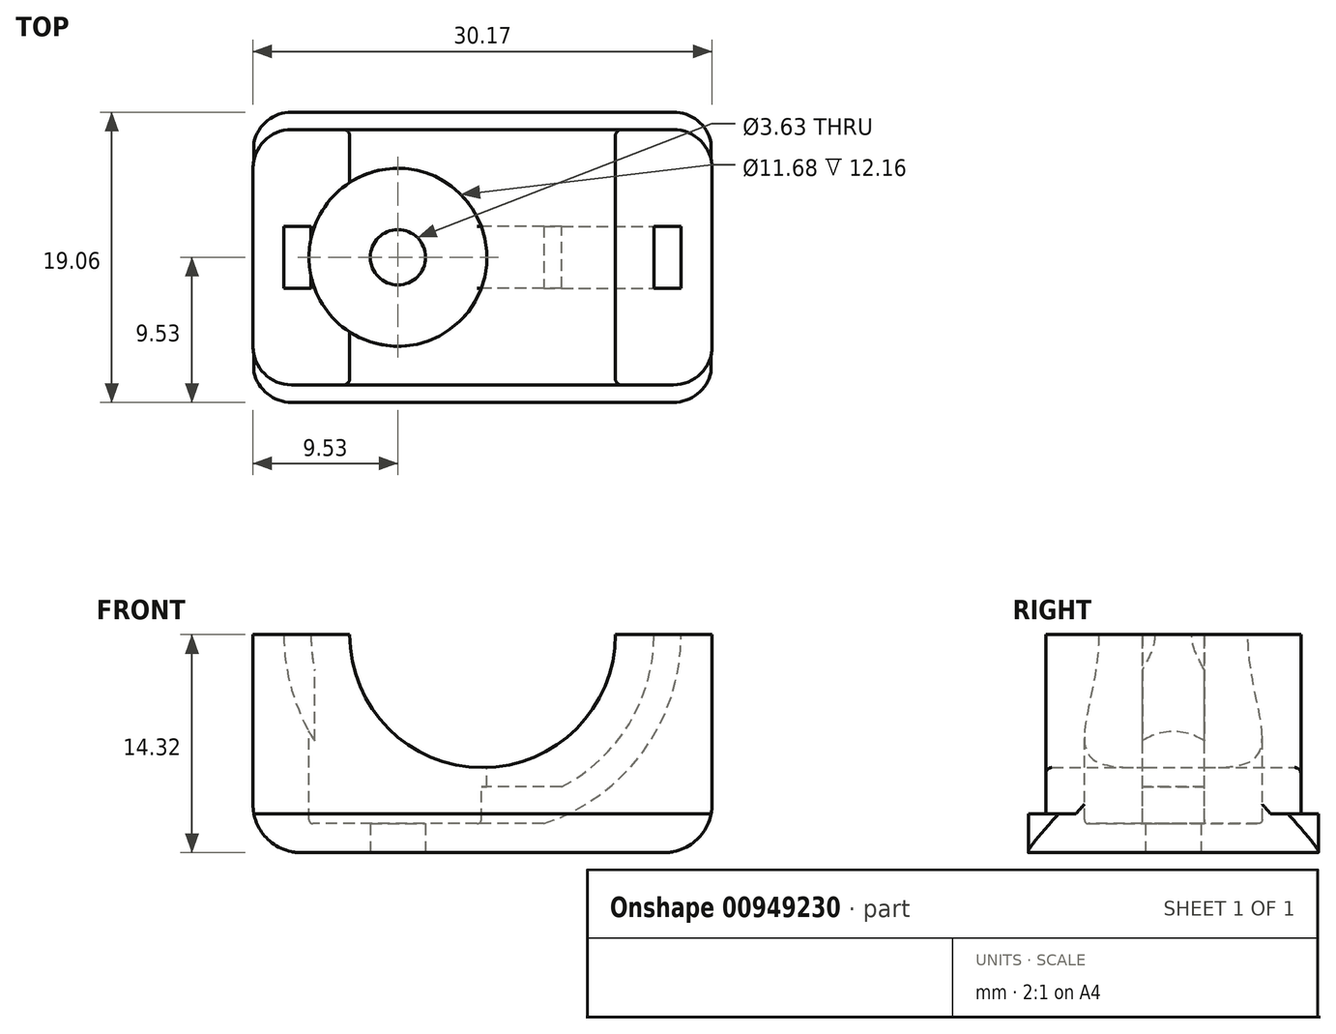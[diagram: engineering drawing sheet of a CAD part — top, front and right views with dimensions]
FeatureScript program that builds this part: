
annotation { "Feature Type Name" : "Feature", "Feature Type Description" : "" }
export const myFeature = defineFeature(function(context is Context, id is Id, definition is map)
    precondition{}
    {
        {
            assignVariable(context, id + "F0", {"name" : "TieWidth", "anyValue" : 4.06 * mm});
        }
        {
            assignVariable(context, id + "F1", {"name" : "RivetThick", "anyValue" : 1.9 * mm});
        }
        {
            var Q0;
            Q0=qCreatedBy(makeId("Top.planeOp"),FACE);
            var sketch = newSketch(context, id + "F2", { "sketchPlane" : qUnion([Q0])});
            skLineSegment(sketch, "E0.bottom", {"start": v(20.64, -9.53) * mm, "end": v(-9.53, -9.53) * mm});
            skLineSegment(sketch, "E0.top", {"start": v(20.64, 9.52) * mm, "end": v(-9.53, 9.52) * mm});
            skLineSegment(sketch, "E0.left", {"start": v(20.64, -9.53) * mm, "end": v(20.64, 9.53) * mm});
            skLineSegment(sketch, "E0.right", {"start": v(-9.53, -9.53) * mm, "end": v(-9.53, 9.53) * mm});
            skPoint(sketch, "E0.middle", {"position": v(0, 0) * mm});
            skPoint(sketch, "E1.visualSharp", {"position": v(-9.53, 9.53) * mm});
            skPoint(sketch, "E2.visualSharp", {"position": v(20.64, 9.53) * mm});
            skPoint(sketch, "E3.visualSharp", {"position": v(20.64, -9.53) * mm});
            skPoint(sketch, "E4.visualSharp", {"position": v(-9.53, -9.53) * mm});
            skCircle(sketch, "E5", {"center": v(0, 0) * mm, "radius": 1.82 * mm});
            skCircle(sketch, "E6", {"center": v(0, 0) * mm, "radius": 5.84 * mm});
            skLineSegment(sketch, "E7", {"start": v(0, 9.52) * mm, "end": v(0, -9.53) * mm, "construction": true});
            skPoint(sketch, "E7.startSnap0", {"position": v(5.56, 9.53) * mm});
            skLineSegment(sketch, "E8", {"start": v(-9.53, 0) * mm, "end": v(20.64, 0) * mm, "construction": true});
            skPoint(sketch, "E9", {"position": v(5.56, 0) * mm});
            skSolve(sketch);
        }
        {
            var Q0;
            Q0 = qSketchRegion(id + "F2", true);
            var Q1;
            Q1=makeQuery(id+"F2.imprint","IMPRINT",FACE,{"disambiguationData":[TD([[makeQuery(id+"F2.imprint","IMPRINT",EDGE,{"derivedFrom":sQuery(id+"F2.wireOp",EDGE,"E5")}),-1.0]])]});
            extrude(context, id + "F3", {"entities" : qUnion([Q0, Q1]), "depth" : 2.54 * mm, "offsetDistance" : 25.4 * mm});
        }
        {
            var Q0;
            Q0=qCreatedBy(makeId("Front.planeOp"),FACE);
            var sketch = newSketch(context, id + "F4", { "sketchPlane" : qUnion([Q0])});
            skArc(sketch, "E10", {"start": v(-3.18, 14.32) * mm, "mid": v(5.56, 5.59) * mm, "end": v(14.29, 14.32) * mm});
            skArc(sketch, "E11", {"start": v(-5.72, 14.32) * mm, "mid": v(-4.08, 8.47) * mm, "end": v(0.36, 4.32) * mm});
            skArc(sketch, "E12", {"start": v(-7.5, 14.32) * mm, "mid": v(-5, 6.64) * mm, "end": v(1.54, 1.9) * mm});
            skLineSegment(sketch, "E13.0", {"start": v(-9.53, 3.17) * mm, "end": v(-9.53, 0) * mm, "construction": true});
            skPoint(sketch, "E14.0", {"position": v(20.64, 1.27) * mm});
            skLineSegment(sketch, "E15.0", {"start": v(20.64, 2.54) * mm, "end": v(20.64, 0) * mm, "construction": true});
            skLineSegment(sketch, "E16", {"start": v(-9.53, 0) * mm, "end": v(-9.53, 14.32) * mm});
            skLineSegment(sketch, "E17", {"start": v(-9.53, 14.32) * mm, "end": v(-7.5, 14.32) * mm});
            skLineSegment(sketch, "E18", {"start": v(20.64, 14.32) * mm, "end": v(20.64, 0) * mm});
            skLineSegment(sketch, "E19.trimOffspring", {"start": v(14.29, 14.32) * mm, "end": v(16.83, 14.32) * mm});
            skLineSegment(sketch, "E20.trimOffspring", {"start": v(18.6, 14.32) * mm, "end": v(20.64, 14.32) * mm});
            skLineSegment(sketch, "E21", {"start": v(-9.53, 0) * mm, "end": v(20.64, 0) * mm});
            skLineSegment(sketch, "E22", {"start": v(10.75, 4.32) * mm, "end": v(0.36, 4.32) * mm});
            skLineSegment(sketch, "E23", {"start": v(9.58, 1.9) * mm, "end": v(1.54, 1.9) * mm});
            skLineSegment(sketch, "E24.trimOffspring", {"start": v(-5.72, 14.32) * mm, "end": v(-3.18, 14.32) * mm});
            skArc(sketch, "E25.trimOffspring", {"start": v(10.75, 4.32) * mm, "mid": v(15.2, 8.47) * mm, "end": v(16.83, 14.32) * mm});
            skArc(sketch, "E26.trimOffspring", {"start": v(9.58, 1.9) * mm, "mid": v(16.1, 6.64) * mm, "end": v(18.6, 14.32) * mm});
            skLineSegment(sketch, "E27.0", {"start": v(-1.73, 1.9) * mm, "end": v(1.73, 1.9) * mm, "construction": true});
            skLineSegment(sketch, "E28", {"start": v(-7.5, 14.32) * mm, "end": v(-5.72, 14.32) * mm});
            skLineSegment(sketch, "E29", {"start": v(16.83, 14.32) * mm, "end": v(18.6, 14.32) * mm});
            skSolve(sketch);
        }
        {
            var Q0;
            {var subQ1=sQuery(id+"F4.wireOp",EDGE,"E12");Q0=makeQuery(id+"F4.imprint","IMPRINT",FACE,{"disambiguationData":[TD([[makeQuery(id+"F4.imprint","IMPRINT",EDGE,{"derivedFrom":subQ1}),-1.0]])]});}
            extrude(context, id + "F5", {"entities" : qUnion([Q0]), "operationType" : NewBodyOperationType.ADD, "endBound" : BoundingType.SYMMETRIC, "depth" : getVariable(context, 'TieWidth'), "offsetDistance" : 25.4 * mm});
        }
        {
            var Q0;
            Q0=makeQuery(id+"F5.opExtrude","CAP_FACE",FACE,{"disambiguationData":[OSD([sQuery(id+"F4.wireOp",EDGE,"E12"),sQuery(id+"F4.wireOp",EDGE,"E16"),sQuery(id+"F4.wireOp",EDGE,"E17"),sQuery(id+"F4.wireOp",EDGE,"E18"),sQuery(id+"F4.wireOp",EDGE,"E20.trimOffspring"),sQuery(id+"F4.wireOp",EDGE,"E21")])],"isStart":false});
            var sketch = newSketch(context, id + "F6", { "sketchPlane" : qUnion([Q0])});
            skLineSegment(sketch, "E30.bottom", {"start": v(-9.53, 14.32) * mm, "end": v(-3.18, 14.32) * mm});
            skLineSegment(sketch, "E30.left", {"start": v(-9.53, 14.32) * mm, "end": v(-9.53, 0) * mm});
            skLineSegment(sketch, "E30.right", {"start": v(20.64, 14.32) * mm, "end": v(20.64, 0) * mm});
            skArc(sketch, "E31.0", {"start": v(-3.18, 14.32) * mm, "mid": v(5.56, 5.59) * mm, "end": v(14.29, 14.32) * mm});
            skLineSegment(sketch, "E32.trimOffspring", {"start": v(14.29, 14.32) * mm, "end": v(20.64, 14.32) * mm});
            skLineSegment(sketch, "E33", {"start": v(-9.53, 0) * mm, "end": v(20.64, 0) * mm});
            skSolve(sketch);
        }
        {
            var Q0;
            Q0 = qSketchRegion(id + "F6", true);
            extrude(context, id + "F7", {"entities" : qUnion([Q0]), "operationType" : NewBodyOperationType.ADD, "depth" : 6.35 * mm, "offsetDistance" : 25.4 * mm});
        }
        {
            var Q0;
            Q0=makeQuery(id+"F4.imprint","IMPRINT",FACE,{"disambiguationData":[TD([[makeQuery(id+"F4.imprint","IMPRINT",EDGE,{"derivedFrom":sQuery(id+"F4.wireOp",EDGE,"E11")}),-1.0]])]});
            extrude(context, id + "F8", {"entities" : qUnion([Q0]), "operationType" : NewBodyOperationType.REMOVE, "endBound" : BoundingType.SYMMETRIC, "oppositeDirection" : true, "depth" : getVariable(context, 'TieWidth'), "offsetDistance" : 25.4 * mm});
        }
        {
            var Q0;
            {var subQ0=sQuery(id+"F4.wireOp",EDGE,"E10");Q0=makeQuery(id+"F4.imprint","IMPRINT",FACE,{"disambiguationData":[TD([[makeQuery(id+"F4.imprint","IMPRINT",EDGE,{"derivedFrom":subQ0}),-1.0]])]});}
            var Q1;
            Q1=makeQuery(id+"F3.opExtrude","SWEPT_BODY",BODY,{"disambiguationData":[OSD([sQuery(id+"F2.wireOp",EDGE,"E0.bottom"),sQuery(id+"F2.wireOp",EDGE,"E0.top"),sQuery(id+"F2.wireOp",EDGE,"E0.left"),sQuery(id+"F2.wireOp",EDGE,"E0.right"),sQuery(id+"F2.wireOp",EDGE,"E1.filletArc"),sQuery(id+"F2.wireOp",EDGE,"E2.filletArc"),sQuery(id+"F2.wireOp",EDGE,"E3.filletArc"),sQuery(id+"F2.wireOp",EDGE,"E4.filletArc"),sQuery(id+"F2.wireOp",EDGE,"E5")])]});
            extrude(context, id + "F9", {"entities" : qUnion([Q0]), "operationType" : NewBodyOperationType.ADD, "endBound" : BoundingType.UP_TO_BODY, "depth" : 6.35 * mm, "endBoundEntityBody" : qUnion([Q1]), "offsetDistance" : 25.4 * mm});
        }
        {
            var Q0;
            Q0=makeQuery(id+"F3.opExtrude","SWEPT_BODY",BODY,{"disambiguationData":[OSD([sQuery(id+"F2.wireOp",EDGE,"E0.bottom"),sQuery(id+"F2.wireOp",EDGE,"E0.top"),sQuery(id+"F2.wireOp",EDGE,"E0.left"),sQuery(id+"F2.wireOp",EDGE,"E0.right"),sQuery(id+"F2.wireOp",EDGE,"E1.filletArc"),sQuery(id+"F2.wireOp",EDGE,"E2.filletArc"),sQuery(id+"F2.wireOp",EDGE,"E3.filletArc"),sQuery(id+"F2.wireOp",EDGE,"E4.filletArc"),sQuery(id+"F2.wireOp",EDGE,"E5")])]});
            var Q1;
            Q1=qCreatedBy(makeId("Front.planeOp"),FACE);
            mirror(context, id + "F10", {"operationType" : NewBodyOperationType.ADD, "entities" : qUnion([Q0]), "mirrorPlane" : qUnion([Q1])});
        }
        {
            var Q0;
            Q0=makeQuery(id+"F2.imprint","IMPRINT",FACE,{"disambiguationData":[TD([[makeQuery(id+"F2.imprint","IMPRINT",EDGE,{"derivedFrom":sQuery(id+"F2.wireOp",EDGE,"E5")}),1.0]])]});
            extrude(context, id + "F11", {"entities" : qUnion([Q0]), "operationType" : NewBodyOperationType.REMOVE, "endBound" : BoundingType.THROUGH_ALL, "depth" : 25.4 * mm, "offsetDistance" : 25.4 * mm});
        }
        {
            var Q0;
            {var subQ0=sQuery(id+"F4.wireOp",EDGE,"E17");var subQ1=makeQuery(id+"F9.boolean.opBoolean","MERGE",FACE,{"derivedFrom":[makeQuery(id+"F7.boolean.opBoolean","MERGE",FACE,{"derivedFrom":[makeQuery(id+"F5.opExtrude","SWEPT_FACE",FACE,{"disambiguationData":[OSD([subQ0])]}),makeQuery(id+"F7.opExtrude","SWEPT_FACE",FACE,{"disambiguationData":[OSD([sQuery(id+"F6.wireOp",EDGE,"E30.bottom")])]})]}),makeQuery(id+"F9.opExtrude","SWEPT_FACE",FACE,{"disambiguationData":[OSD([subQ0])]})]});Q0=makeQuery(id+"F10.boolean.opBoolean","MERGE",FACE,{"derivedFrom":[subQ1,makeQuery(id+"F10.opPattern","COPY",FACE,{"derivedFrom":subQ1,"instanceName":"1"})]});}
            var sketch = newSketch(context, id + "F12", { "sketchPlane" : qUnion([Q0])});
            skCircle(sketch, "E34.0", {"center": v(0, 0) * mm, "radius": 5.84 * mm});
            skSolve(sketch);
        }
        {
            var Q0;
            Q0 = qSketchRegion(id + "F12", true);
            var Q1;
            Q1=makeQuery(id+"F5.boolean.opBoolean","MERGE",FACE,{"derivedFrom":[makeQuery(id+"F3.opExtrude","CAP_FACE",FACE,{"disambiguationData":[OSD([sQuery(id+"F2.wireOp",EDGE,"E0.bottom"),sQuery(id+"F2.wireOp",EDGE,"E0.top"),sQuery(id+"F2.wireOp",EDGE,"E0.left"),sQuery(id+"F2.wireOp",EDGE,"E0.right"),sQuery(id+"F2.wireOp",EDGE,"E5")])],"isStart":true}),makeQuery(id+"F5.opExtrude","SWEPT_FACE",FACE,{"disambiguationData":[OSD([sQuery(id+"F4.wireOp",EDGE,"E21")])]})]});
            extrude(context, id + "F13", {"entities" : qUnion([Q0]), "operationType" : NewBodyOperationType.REMOVE, "endBound" : BoundingType.UP_TO_SURFACE, "oppositeDirection" : true, "depth" : 25.4 * mm, "endBoundEntityFace" : qUnion([Q1]), "hasOffset" : true, "offsetDistance" : getVariable(context, 'RivetThick')});
        }
        {
            var Q0;
            Q0=makeQuery(id+"F3.opExtrude","SWEPT_EDGE",EDGE,{"disambiguationData":[OSD([sQuery(id+"F2.wireOp",EDGE,"E0.top"),sQuery(id+"F2.wireOp",EDGE,"E0.left")])]});
            var Q1;
            Q1=makeQuery(id+"F3.opExtrude","SWEPT_EDGE",EDGE,{"disambiguationData":[OSD([sQuery(id+"F2.wireOp",EDGE,"E0.top"),sQuery(id+"F2.wireOp",EDGE,"E0.right")])]});
            var Q2;
            Q2=makeQuery(id+"F3.opExtrude","SWEPT_EDGE",EDGE,{"disambiguationData":[OSD([sQuery(id+"F2.wireOp",EDGE,"E0.bottom"),sQuery(id+"F2.wireOp",EDGE,"E0.left")])]});
            var Q3;
            Q3=makeQuery(id+"F3.opExtrude","SWEPT_EDGE",EDGE,{"disambiguationData":[OSD([sQuery(id+"F2.wireOp",EDGE,"E0.bottom"),sQuery(id+"F2.wireOp",EDGE,"E0.right")])]});
            fillet(context, id + "F14", {"entities" : qUnion([Q0, Q1, Q2, Q3]), "radius" : 2.54 * mm, "tangentPropagation" : true, "allowEdgeOverflow" : false});
        }
        {
            var Q0;
            Q0=makeQuery(id+"F7.opExtrude","CAP_EDGE",EDGE,{"disambiguationData":[OSD([sQuery(id+"F6.wireOp",EDGE,"E31.0")])],"isStart":false});
            var Q1;
            Q1=makeQuery(id+"F10.opPattern","COPY",EDGE,{"derivedFrom":makeQuery(id+"F7.opExtrude","CAP_EDGE",EDGE,{"disambiguationData":[OSD([sQuery(id+"F6.wireOp",EDGE,"E31.0")])],"isStart":false}),"instanceName":"1"});
            fillet(context, id + "F15", {"entities" : qUnion([Q0, Q1]), "radius" : 0.4 * mm, "tangentPropagation" : true, "allowEdgeOverflow" : false});
        }
        {
            var Q0;
            Q0=makeQuery(id+"F13.boolean.opBoolean","COPY",EDGE,{"derivedFrom":makeQuery(id+"F13.opExtrude","CAP_EDGE",EDGE,{"disambiguationData":[OSD([sQuery(id+"F12.wireOp",EDGE,"E34.0")])],"isStart":false})});
            fillet(context, id + "F16", {"entities" : qUnion([Q0]), "radius" : 0.25 * mm, "allowEdgeOverflow" : false});
        }
        {
            var Q0;
            Q0=makeQuery(id+"F14.opFillet","BLEND_EDGE",EDGE,{"blendedFrom":[makeQuery(id+"F3.opExtrude","SWEPT_EDGE",EDGE,{"disambiguationData":[OSD([sQuery(id+"F2.wireOp",EDGE,"E0.bottom"),sQuery(id+"F2.wireOp",EDGE,"E0.right")])]}),makeQuery(id+"F7.opExtrude","CAP_FACE",FACE,{"disambiguationData":[OSD([sQuery(id+"F6.wireOp",EDGE,"E30.bottom"),sQuery(id+"F6.wireOp",EDGE,"E30.left"),sQuery(id+"F6.wireOp",EDGE,"E30.right"),sQuery(id+"F6.wireOp",EDGE,"E31.0"),sQuery(id+"F6.wireOp",EDGE,"E32.trimOffspring"),sQuery(id+"F6.wireOp",EDGE,"E33")])],"isStart":false})],"blendedInto":[makeQuery(id+"F7.opExtrude","CAP_FACE",FACE,{"disambiguationData":[OSD([sQuery(id+"F6.wireOp",EDGE,"E30.bottom"),sQuery(id+"F6.wireOp",EDGE,"E30.left"),sQuery(id+"F6.wireOp",EDGE,"E30.right"),sQuery(id+"F6.wireOp",EDGE,"E31.0"),sQuery(id+"F6.wireOp",EDGE,"E32.trimOffspring"),sQuery(id+"F6.wireOp",EDGE,"E33")])],"isStart":false})]});
            var Q1;
            Q1=makeQuery(id+"F14.opFillet","BLEND_EDGE",EDGE,{"blendedFrom":[makeQuery(id+"F3.opExtrude","SWEPT_EDGE",EDGE,{"disambiguationData":[OSD([sQuery(id+"F2.wireOp",EDGE,"E0.bottom"),sQuery(id+"F2.wireOp",EDGE,"E0.left")])]}),makeQuery(id+"F7.opExtrude","CAP_FACE",FACE,{"disambiguationData":[OSD([sQuery(id+"F6.wireOp",EDGE,"E30.bottom"),sQuery(id+"F6.wireOp",EDGE,"E30.left"),sQuery(id+"F6.wireOp",EDGE,"E30.right"),sQuery(id+"F6.wireOp",EDGE,"E31.0"),sQuery(id+"F6.wireOp",EDGE,"E32.trimOffspring"),sQuery(id+"F6.wireOp",EDGE,"E33")])],"isStart":false})],"blendedInto":[makeQuery(id+"F7.opExtrude","CAP_FACE",FACE,{"disambiguationData":[OSD([sQuery(id+"F6.wireOp",EDGE,"E30.bottom"),sQuery(id+"F6.wireOp",EDGE,"E30.left"),sQuery(id+"F6.wireOp",EDGE,"E30.right"),sQuery(id+"F6.wireOp",EDGE,"E31.0"),sQuery(id+"F6.wireOp",EDGE,"E32.trimOffspring"),sQuery(id+"F6.wireOp",EDGE,"E33")])],"isStart":false})]});
            var Q2;
            Q2=makeQuery(id+"F14.opFillet","BLEND_EDGE",EDGE,{"blendedFrom":[makeQuery(id+"F3.opExtrude","SWEPT_EDGE",EDGE,{"disambiguationData":[OSD([sQuery(id+"F2.wireOp",EDGE,"E0.top"),sQuery(id+"F2.wireOp",EDGE,"E0.left")])]}),makeQuery(id+"F10.opPattern","COPY",FACE,{"derivedFrom":makeQuery(id+"F7.opExtrude","CAP_FACE",FACE,{"disambiguationData":[OSD([sQuery(id+"F6.wireOp",EDGE,"E30.bottom"),sQuery(id+"F6.wireOp",EDGE,"E30.left"),sQuery(id+"F6.wireOp",EDGE,"E30.right"),sQuery(id+"F6.wireOp",EDGE,"E31.0"),sQuery(id+"F6.wireOp",EDGE,"E32.trimOffspring"),sQuery(id+"F6.wireOp",EDGE,"E33")])],"isStart":false}),"instanceName":"1"})],"blendedInto":[makeQuery(id+"F10.opPattern","COPY",FACE,{"derivedFrom":makeQuery(id+"F7.opExtrude","CAP_FACE",FACE,{"disambiguationData":[OSD([sQuery(id+"F6.wireOp",EDGE,"E30.bottom"),sQuery(id+"F6.wireOp",EDGE,"E30.left"),sQuery(id+"F6.wireOp",EDGE,"E30.right"),sQuery(id+"F6.wireOp",EDGE,"E31.0"),sQuery(id+"F6.wireOp",EDGE,"E32.trimOffspring"),sQuery(id+"F6.wireOp",EDGE,"E33")])],"isStart":false}),"instanceName":"1"})]});
            var Q3;
            Q3=makeQuery(id+"F14.opFillet","BLEND_EDGE",EDGE,{"blendedFrom":[makeQuery(id+"F3.opExtrude","SWEPT_EDGE",EDGE,{"disambiguationData":[OSD([sQuery(id+"F2.wireOp",EDGE,"E0.top"),sQuery(id+"F2.wireOp",EDGE,"E0.right")])]}),makeQuery(id+"F10.opPattern","COPY",FACE,{"derivedFrom":makeQuery(id+"F7.opExtrude","CAP_FACE",FACE,{"disambiguationData":[OSD([sQuery(id+"F6.wireOp",EDGE,"E30.bottom"),sQuery(id+"F6.wireOp",EDGE,"E30.left"),sQuery(id+"F6.wireOp",EDGE,"E30.right"),sQuery(id+"F6.wireOp",EDGE,"E31.0"),sQuery(id+"F6.wireOp",EDGE,"E32.trimOffspring"),sQuery(id+"F6.wireOp",EDGE,"E33")])],"isStart":false}),"instanceName":"1"})],"blendedInto":[makeQuery(id+"F10.opPattern","COPY",FACE,{"derivedFrom":makeQuery(id+"F7.opExtrude","CAP_FACE",FACE,{"disambiguationData":[OSD([sQuery(id+"F6.wireOp",EDGE,"E30.bottom"),sQuery(id+"F6.wireOp",EDGE,"E30.left"),sQuery(id+"F6.wireOp",EDGE,"E30.right"),sQuery(id+"F6.wireOp",EDGE,"E31.0"),sQuery(id+"F6.wireOp",EDGE,"E32.trimOffspring"),sQuery(id+"F6.wireOp",EDGE,"E33")])],"isStart":false}),"instanceName":"1"})]});
            fillet(context, id + "F17", {"entities" : qUnion([Q0, Q1, Q2, Q3]), "radius" : 2.54 * mm, "tangentPropagation" : true, "allowEdgeOverflow" : false});
        }
        {
            var Q0;
            Q0=makeQuery(id+"F3.opExtrude","CAP_EDGE",EDGE,{"disambiguationData":[OSD([sQuery(id+"F2.wireOp",EDGE,"E0.left")])],"isStart":true});
            var Q1;
            Q1=makeQuery(id+"F3.opExtrude","CAP_EDGE",EDGE,{"disambiguationData":[OSD([sQuery(id+"F2.wireOp",EDGE,"E0.right")])],"isStart":true});
            fillet(context, id + "F18", {"entities" : qUnion([Q0, Q1]), "radius" : 3.17 * mm, "allowEdgeOverflow" : false});
        }
    });
